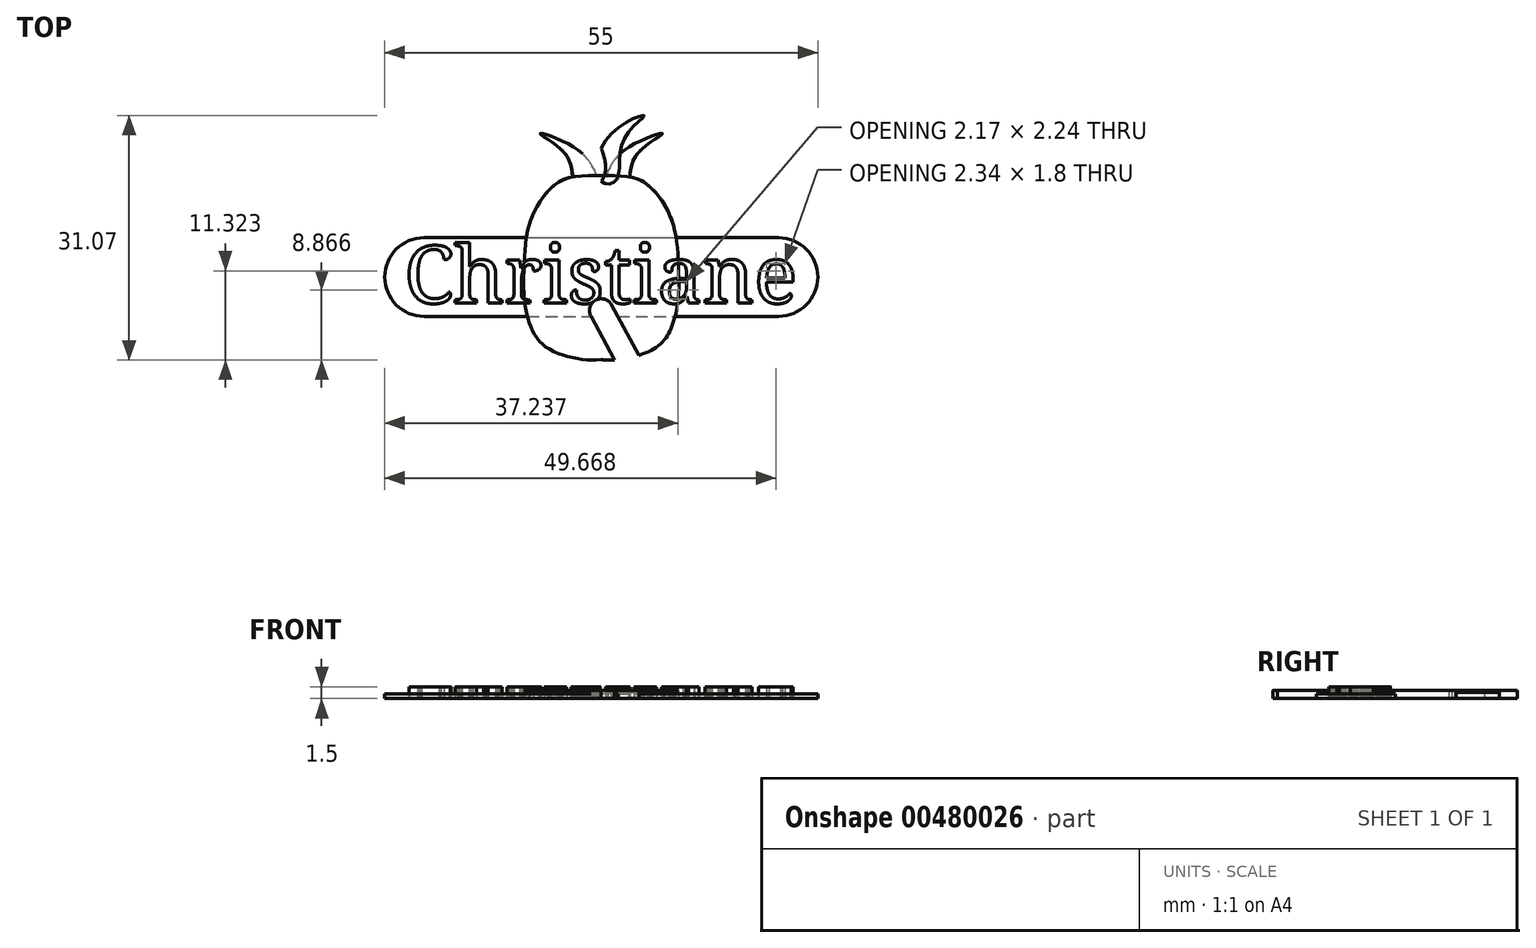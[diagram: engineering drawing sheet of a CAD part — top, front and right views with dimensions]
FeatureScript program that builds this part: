
annotation { "Feature Type Name" : "Feature", "Feature Type Description" : "" }
export const myFeature = defineFeature(function(context is Context, id is Id, definition is map)
    precondition{}
    {
        {
            var Q0;
            Q0=qCreatedBy(makeId("Top.planeOp"),FACE);
            var sketch = newSketch(context, id + "F0", { "sketchPlane" : qUnion([Q0])});
            skText(sketch, "E0", { "text": "Christiane", "fontName": "NotoSerif-Regular.ttf"});
            const initialGuessF0  = {"E0": [-0.025, -0.00732, 1, 0, 0.00732]};
            skSetInitialGuess(sketch, initialGuessF0);
            skSolve(sketch);
        }
        {
            var Q0;
            Q0 = qSketchRegion(id + "F0", true);
            extrude(context, id + "F1", {"entities" : qUnion([Q0]), "depth" : 1.5 * mm, "offsetDistance" : 25 * mm});
        }
        {
            var Q0;
            Q0=qCreatedBy(makeId("Top.planeOp"),FACE);
            var sketch = newSketch(context, id + "F2", { "sketchPlane" : qUnion([Q0])});
            skFitSpline(sketch, "E1", {"points": [v(0, -14.5) * mm, v(-3.65, -14.24) * mm, v(-7.11, -12.83) * mm, v(-8.78, -10.71) * mm, v(-9.74, -7.05) * mm, v(-9.8, -2.69) * mm, v(-9.49, 1.16) * mm, v(-8.52, 4.24) * mm, v(-6.73, 6.94) * mm, v(-4.16, 8.6) * mm, v(0, 8.86) * mm], "startDerivative": vector(-36.01, -3.1) * mm, "endDerivative": vector(39.07, 0.66) * mm});
            skFitSpline(sketch, "E2.MirrorCS", {"points": [v(0, -14.5) * mm, v(3.65, -14.24) * mm, v(7.11, -12.83) * mm, v(8.78, -10.71) * mm, v(9.74, -7.05) * mm, v(9.8, -2.69) * mm, v(9.49, 1.16) * mm, v(8.52, 4.24) * mm, v(6.73, 6.94) * mm, v(4.16, 8.6) * mm, v(0, 8.86) * mm], "startDerivative": vector(36.01, -3.1) * mm, "endDerivative": vector(-39.07, 0.66) * mm});
            skSolve(sketch);
        }
        {
            var Q0;
            Q0=makeQuery(id+"F2.imprint","IMPRINT",FACE,{"disambiguationData":[TD([[makeQuery(id+"F2.imprint","IMPRINT",EDGE,{"derivedFrom":sQuery(id+"F2.wireOp",EDGE,"E1")}),-1.0]])]});
            extrude(context, id + "F3", {"entities" : qUnion([Q0]), "depth" : 1 * mm, "offsetDistance" : 25 * mm});
        }
        {
            var Q0;
            Q0=qCreatedBy(makeId("Top.planeOp"),FACE);
            var sketch = newSketch(context, id + "F4", { "sketchPlane" : qUnion([Q0])});
            skFitSpline(sketch, "E3", {"points": [v(-3.62, 8.13) * mm, v(-4.76, 11.85) * mm, v(-7.76, 14.23) * mm, v(-3.16, 12.26) * mm, v(-0.47, 8.54) * mm], "startDerivative": vector(-0.55, 16.12) * mm, "endDerivative": vector(6.29, -15.12) * mm});
            skLineSegment(sketch, "E4", {"start": v(-3.62, 8.13) * mm, "end": v(-0.47, 8.54) * mm});
            skFitSpline(sketch, "E5.MirrorCS", {"points": [v(3.62, 8.13) * mm, v(4.76, 11.85) * mm, v(7.76, 14.23) * mm, v(3.16, 12.26) * mm, v(0.47, 8.54) * mm], "startDerivative": vector(0.55, 16.12) * mm, "endDerivative": vector(-6.29, -15.12) * mm});
            skLineSegment(sketch, "E6", {"start": v(0.47, 8.54) * mm, "end": v(3.62, 8.13) * mm});
            skSolve(sketch);
        }
        {
            var Q0;
            Q0=makeQuery(id+"F4.imprint","IMPRINT",FACE,{"disambiguationData":[TD([[makeQuery(id+"F4.imprint","IMPRINT",EDGE,{"derivedFrom":sQuery(id+"F4.wireOp",EDGE,"E3")}),-1.0]])]});
            var Q1;
            Q1=makeQuery(id+"F4.imprint","IMPRINT",FACE,{"disambiguationData":[TD([[makeQuery(id+"F4.imprint","IMPRINT",EDGE,{"derivedFrom":sQuery(id+"F4.wireOp",EDGE,"E5.MirrorCS")}),1.0]])]});
            extrude(context, id + "F5", {"entities" : qUnion([Q0, Q1]), "operationType" : NewBodyOperationType.ADD, "depth" : 0.8 * mm, "offsetDistance" : 25 * mm});
        }
        {
            var Q0;
            Q0=qCreatedBy(makeId("Top.planeOp"),FACE);
            var sketch = newSketch(context, id + "F6", { "sketchPlane" : qUnion([Q0])});
            skFitSpline(sketch, "E7", {"points": [v(-1.9, 8.32) * mm, v(-2.9, 13.55) * mm, v(-5.45, 16.5) * mm, v(-0.96, 13.88) * mm, v(0, 8.18) * mm, v(-1.9, 8.32) * mm]});
            skFitSpline(sketch, "E8.MirrorC", {"points": [v(1.9, 8.32) * mm, v(2.9, 13.55) * mm, v(5.45, 16.5) * mm, v(0.96, 13.88) * mm, v(0, 8.18) * mm, v(1.9, 8.32) * mm]});
            skSolve(sketch);
        }
        {
            var Q0;
            {var subQ0=sQuery(id+"F6.wireOp",EDGE,"E8.MirrorC");var subQ1=sQuery(id+"F6.wireOp",EDGE,"E7");var subQ2=makeQuery(id+"F6.imprint","INTERSECT",VERTEX,{"disambiguationData":[OD(0.0)],"derivedFrom":[subQ1,subQ0]});Q0=makeQuery(id+"F6.imprint","IMPRINT",FACE,{"disambiguationData":[TD([[makeQuery(id+"F6.imprint","IMPRINT",EDGE,{"disambiguationData":[TD([[subQ2,-1.0]])],"derivedFrom":subQ1}),-1.0]])]});}
            var Q1;
            {var subQ0=sQuery(id+"F6.wireOp",EDGE,"E8.MirrorC");var subQ1=sQuery(id+"F6.wireOp",EDGE,"E7");var subQ2=makeQuery(id+"F6.imprint","INTERSECT",VERTEX,{"disambiguationData":[OD(0.0)],"derivedFrom":[subQ1,subQ0]});Q1=makeQuery(id+"F6.imprint","IMPRINT",FACE,{"disambiguationData":[TD([[makeQuery(id+"F6.imprint","IMPRINT",EDGE,{"disambiguationData":[TD([[subQ2,1.0]])],"derivedFrom":subQ1}),1.0]])]});}
            extrude(context, id + "F7", {"entities" : qUnion([Q0, Q1]), "depth" : 1 * mm, "offsetDistance" : 25 * mm});
        }
        {
            var Q0;
            Q0=qCreatedBy(makeId("Top.planeOp"),FACE);
            var sketch = newSketch(context, id + "F8", { "sketchPlane" : qUnion([Q0])});
            skLineSegment(sketch, "E9.bottom", {"start": v(-22.5, 1) * mm, "end": v(22.5, 1) * mm});
            skLineSegment(sketch, "E9.top", {"start": v(-22.5, -9) * mm, "end": v(22.5, -9) * mm});
            skArc(sketch, "E10", {"start": v(-22.5, -9) * mm, "mid": v(-27.5, -4) * mm, "end": v(-22.5, 1) * mm});
            skArc(sketch, "E11", {"start": v(22.5, -9) * mm, "mid": v(27.5, -4) * mm, "end": v(22.5, 1) * mm});
            skSolve(sketch);
        }
        {
            var Q0;
            Q0=makeQuery(id+"F8.imprint","IMPRINT",FACE,{"disambiguationData":[TD([[makeQuery(id+"F8.imprint","IMPRINT",EDGE,{"derivedFrom":sQuery(id+"F8.wireOp",EDGE,"E9.bottom")}),-1.0]])]});
            extrude(context, id + "F9", {"entities" : qUnion([Q0]), "depth" : 0.6 * mm, "offsetDistance" : 25 * mm});
        }
        {
            var Q0;
            Q0=qCreatedBy(makeId("Top.planeOp"),FACE);
            var sketch = newSketch(context, id + "F10", { "sketchPlane" : qUnion([Q0])});
            skLineSegment(sketch, "E12", {"start": v(3.92, -18.7) * mm, "end": v(-1.32, -8.97) * mm});
            skLineSegment(sketch, "E13", {"start": v(-1.32, -8.97) * mm, "end": v(1.32, -7.55) * mm, "construction": true});
            skLineSegment(sketch, "E14", {"start": v(1.32, -7.55) * mm, "end": v(6.54, -17.23) * mm});
            skLineSegment(sketch, "E15", {"start": v(6.54, -17.23) * mm, "end": v(3.92, -18.7) * mm});
            skArc(sketch, "E16", {"start": v(-1.32, -8.97) * mm, "mid": v(-0.71, -6.94) * mm, "end": v(1.32, -7.55) * mm});
            skSolve(sketch);
        }
        {
            var Q0;
            Q0=makeQuery(id+"F10.imprint","IMPRINT",FACE,{"disambiguationData":[TD([[makeQuery(id+"F10.imprint","IMPRINT",EDGE,{"derivedFrom":sQuery(id+"F10.wireOp",EDGE,"E12")}),-1.0]])]});
            extrude(context, id + "F11", {"entities" : qUnion([Q0]), "operationType" : NewBodyOperationType.REMOVE, "depth" : 25 * mm, "offsetDistance" : 25 * mm});
        }
    });
